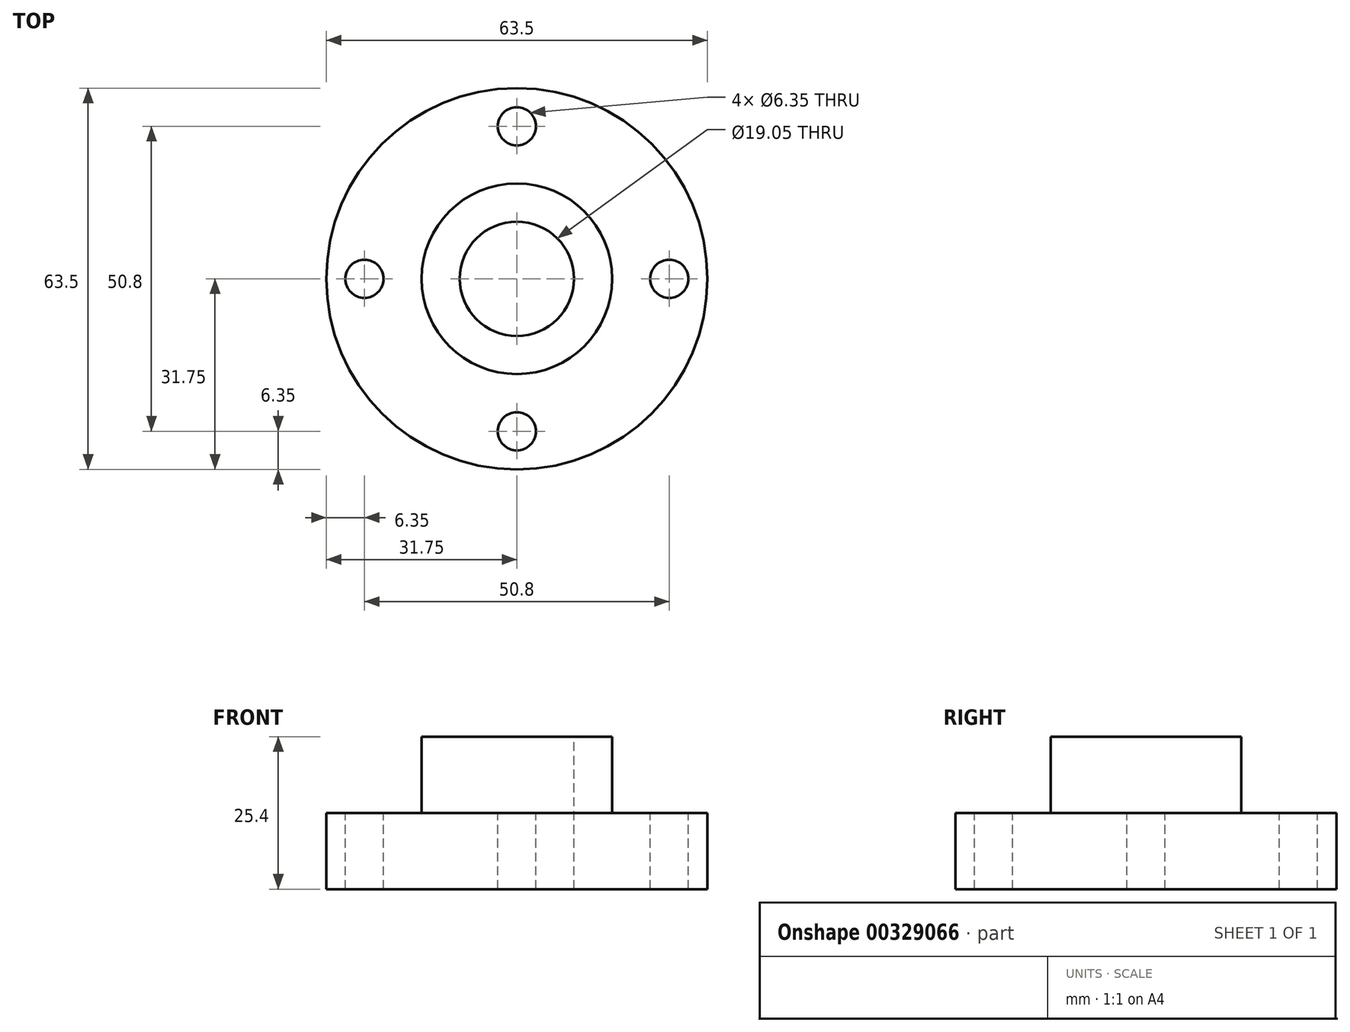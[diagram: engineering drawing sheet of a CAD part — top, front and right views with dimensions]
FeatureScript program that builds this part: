
annotation { "Feature Type Name" : "Feature", "Feature Type Description" : "" }
export const myFeature = defineFeature(function(context is Context, id is Id, definition is map)
    precondition{}
    {
        {
            var Q0;
            Q0=qCreatedBy(makeId("Top.planeOp"),FACE);
            var sketch = newSketch(context, id + "F0", { "sketchPlane" : qUnion([Q0])});
            skCircle(sketch, "E0", {"center": v(0, 0) * mm, "radius": 31.75 * mm});
            skSolve(sketch);
        }
        {
            var Q0;
            Q0 = qSketchRegion(id + "F0", true);
            extrude(context, id + "F1", {"entities" : qUnion([Q0]), "depth" : 12.7 * mm});
        }
        {
            var Q0;
            Q0=makeQuery(id+"F1.opExtrude","CAP_FACE",FACE,{"disambiguationData":[OSD([sQuery(id+"F0.wireOp",EDGE,"E0")])],"isStart":false});
            var sketch = newSketch(context, id + "F2", { "sketchPlane" : qUnion([Q0])});
            skCircle(sketch, "E1", {"center": v(0, 0) * mm, "radius": 15.88 * mm});
            skSolve(sketch);
        }
        {
            var Q0;
            Q0 = qSketchRegion(id + "F2", true);
            extrude(context, id + "F3", {"entities" : qUnion([Q0]), "operationType" : NewBodyOperationType.ADD, "depth" : 12.7 * mm});
        }
        {
            var Q0;
            Q0=makeQuery(id+"F1.opExtrude","CAP_FACE",FACE,{"disambiguationData":[OSD([sQuery(id+"F0.wireOp",EDGE,"E0")])],"isStart":false});
            var sketch = newSketch(context, id + "F4", { "sketchPlane" : qUnion([Q0])});
            skCircle(sketch, "E2", {"center": v(0, 25.4) * mm, "radius": 3.18 * mm});
            skCircle(sketch, "E3", {"center": v(25.4, 0) * mm, "radius": 3.18 * mm});
            skCircle(sketch, "E4", {"center": v(0, -25.4) * mm, "radius": 3.18 * mm});
            skCircle(sketch, "E5", {"center": v(-25.4, 0) * mm, "radius": 3.18 * mm});
            skSolve(sketch);
        }
        {
            var Q0;
            Q0 = qSketchRegion(id + "F4", true);
            extrude(context, id + "F5", {"entities" : qUnion([Q0]), "operationType" : NewBodyOperationType.REMOVE, "endBound" : BoundingType.THROUGH_ALL, "oppositeDirection" : true, "depth" : 25.4 * mm});
        }
        {
            var Q0;
            Q0=makeQuery(id+"F3.opExtrude","CAP_FACE",FACE,{"disambiguationData":[OSD([sQuery(id+"F2.wireOp",EDGE,"E1")])],"isStart":false});
            var sketch = newSketch(context, id + "F6", { "sketchPlane" : qUnion([Q0])});
            skCircle(sketch, "E6", {"center": v(0, 0) * mm, "radius": 9.53 * mm});
            skSolve(sketch);
        }
        {
            var Q0;
            Q0 = qSketchRegion(id + "F6", true);
            extrude(context, id + "F7", {"entities" : qUnion([Q0]), "operationType" : NewBodyOperationType.REMOVE, "endBound" : BoundingType.THROUGH_ALL, "oppositeDirection" : true, "depth" : 25.4 * mm});
        }
    });
